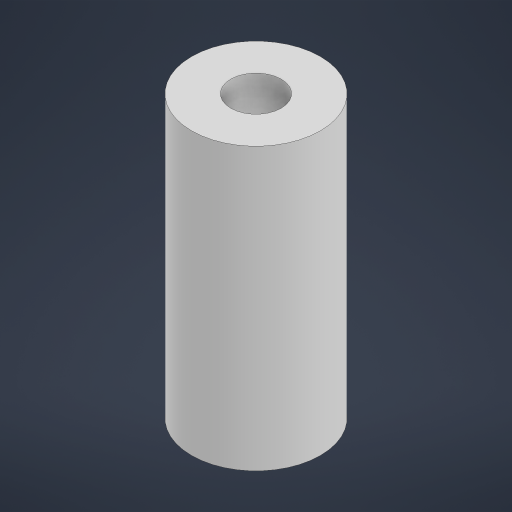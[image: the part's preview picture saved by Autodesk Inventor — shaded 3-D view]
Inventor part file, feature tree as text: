
AUTODESK INVENTOR PART (.ipt)
format: ipt  version: 2024.3 (Build 283343000, 343)  size: 156,672 bytes
history: native  units: in
note: dims shown in document units (in); Inventor stores cm internally (conversion verified against a paired STEP export)
features: extrude x1, sketch x1
ambient origin geometry x8: Origin, YZ Plane, XZ Plane, XY Plane, X Axis, Y Axis, Z Axis, Center Point
bodies: Solid1 (feature_tree)
feature tree (2):
  extrude  "Extrusion1"  Depth=1.092in
  sketch  "Sketch1"  dims[d0=0.5in d1=0.196in d2=1.092in d3=0.0in]
